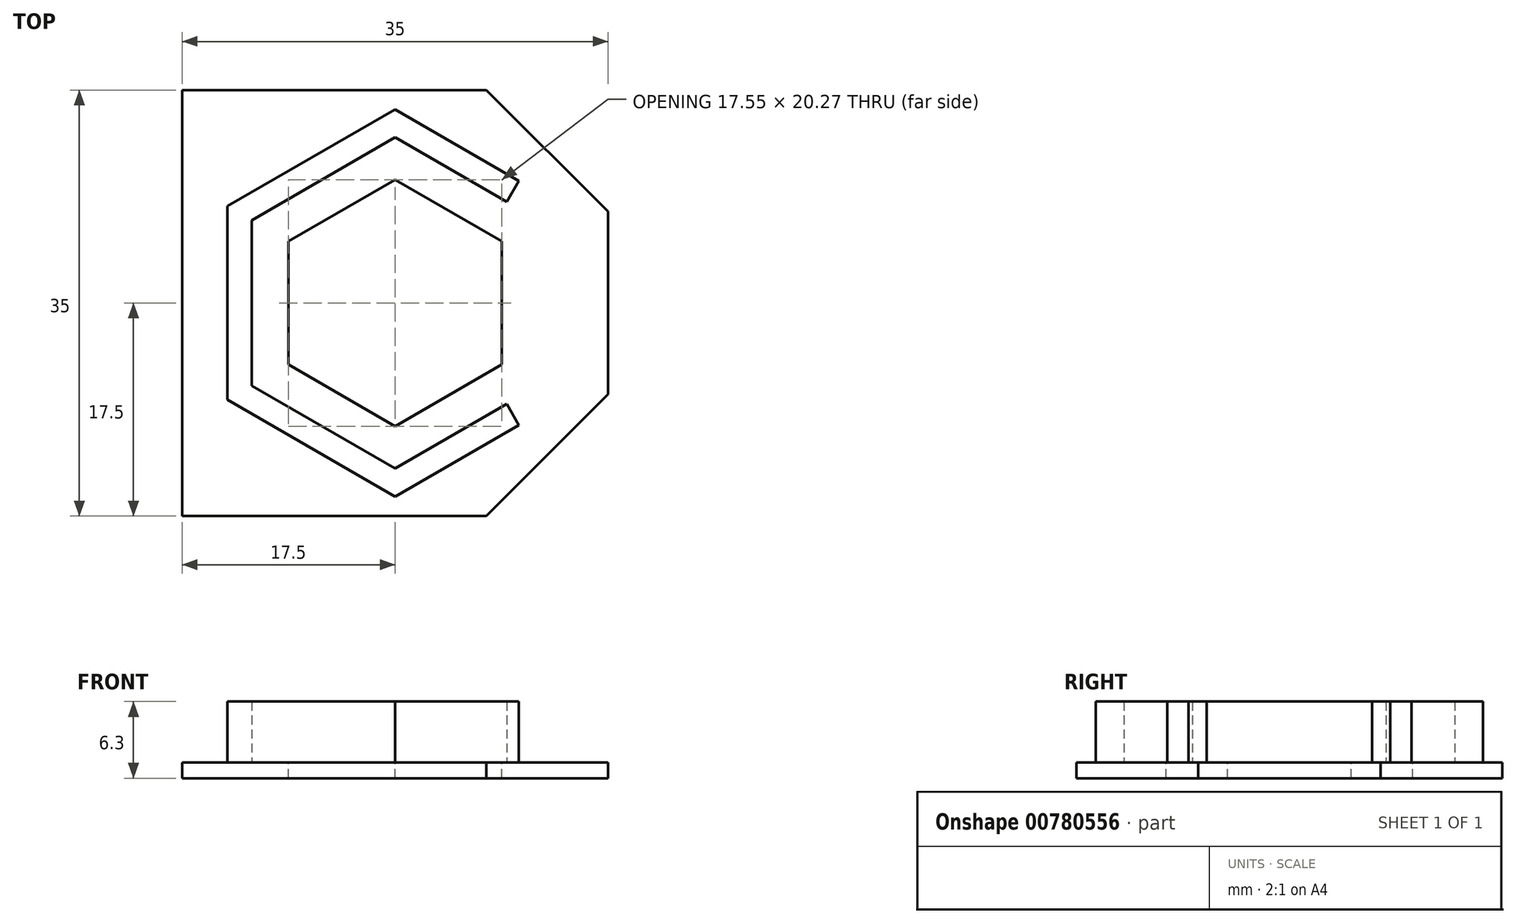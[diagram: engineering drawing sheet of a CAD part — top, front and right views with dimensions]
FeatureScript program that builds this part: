
annotation { "Feature Type Name" : "Feature", "Feature Type Description" : "" }
export const myFeature = defineFeature(function(context is Context, id is Id, definition is map)
    precondition{}
    {
        {
            var Q0;
            Q0=qCreatedBy(makeId("Top.planeOp"),FACE);
            var sketch = newSketch(context, id + "F0", { "sketchPlane" : qUnion([Q0])});
            skLineSegment(sketch, "E0.bottom", {"start": v(0, 0) * mm, "end": v(35, 0) * mm});
            skLineSegment(sketch, "E0.top", {"start": v(0, 35) * mm, "end": v(35, 35) * mm});
            skLineSegment(sketch, "E0.left", {"start": v(0, 0) * mm, "end": v(0, 35) * mm});
            skLineSegment(sketch, "E0.right", {"start": v(35, 0) * mm, "end": v(35, 35) * mm});
            skSolve(sketch);
        }
        {
            var Q0;
            Q0=makeQuery(id+"F0.imprint","IMPRINT",FACE,{"disambiguationData":[TD([[makeQuery(id+"F0.imprint","IMPRINT",EDGE,{"derivedFrom":sQuery(id+"F0.wireOp",EDGE,"E0.bottom")}),1.0]])]});
            extrude(context, id + "F1", {"entities" : qUnion([Q0]), "depth" : 2.6 / 2 * mm, "offsetDistance" : 25 * mm});
        }
        {
            var Q0;
            Q0=makeQuery(id+"F1.opExtrude","CAP_FACE",FACE,{"disambiguationData":[OSD([sQuery(id+"F0.wireOp",EDGE,"E0.bottom"),sQuery(id+"F0.wireOp",EDGE,"E0.top"),sQuery(id+"F0.wireOp",EDGE,"E0.left"),sQuery(id+"F0.wireOp",EDGE,"E0.right")])],"isStart":false});
            var sketch = newSketch(context, id + "F2", { "sketchPlane" : qUnion([Q0])});
            skCircle(sketch, "E1.cCircle", {"center": v(17.5, 17.5) * mm, "radius": 8.78 * mm, "construction": true});
            skLineSegment(sketch, "E1.0", {"start": v(17.5, 27.63) * mm, "end": v(26.28, 22.57) * mm});
            skLineSegment(sketch, "E1.1", {"start": v(26.27, 22.57) * mm, "end": v(26.27, 12.43) * mm});
            skLineSegment(sketch, "E1.2", {"start": v(26.27, 12.43) * mm, "end": v(17.5, 7.37) * mm});
            skLineSegment(sketch, "E1.3", {"start": v(17.5, 7.37) * mm, "end": v(8.73, 12.43) * mm});
            skLineSegment(sketch, "E1.4", {"start": v(8.73, 12.43) * mm, "end": v(8.73, 22.57) * mm});
            skLineSegment(sketch, "E1.5", {"start": v(8.73, 22.57) * mm, "end": v(17.5, 27.63) * mm});
            skPoint(sketch, "E1.0.midPoint", {"position": v(21.89, 25.1) * mm});
            skLineSegment(sketch, "E2.0", {"start": v(5.73, 24.3) * mm, "end": v(17.5, 31.1) * mm});
            skLineSegment(sketch, "E2.1", {"start": v(29.28, 24.3) * mm, "end": v(29.28, 10.7) * mm});
            skLineSegment(sketch, "E2.2", {"start": v(29.28, 10.7) * mm, "end": v(17.5, 3.9) * mm});
            skLineSegment(sketch, "E2.3", {"start": v(17.5, 31.1) * mm, "end": v(29.28, 24.3) * mm});
            skLineSegment(sketch, "E2.4", {"start": v(17.5, 3.9) * mm, "end": v(5.73, 10.7) * mm});
            skLineSegment(sketch, "E2.5", {"start": v(5.73, 10.7) * mm, "end": v(5.73, 24.3) * mm});
            skLineSegment(sketch, "E3.0", {"start": v(3.73, 25.45) * mm, "end": v(17.5, 33.4) * mm});
            skLineSegment(sketch, "E3.1", {"start": v(31.28, 25.45) * mm, "end": v(31.28, 9.55) * mm});
            skLineSegment(sketch, "E3.2", {"start": v(31.27, 9.55) * mm, "end": v(17.5, 1.6) * mm});
            skLineSegment(sketch, "E3.3", {"start": v(17.5, 33.4) * mm, "end": v(31.28, 25.45) * mm});
            skLineSegment(sketch, "E3.4", {"start": v(17.5, 1.6) * mm, "end": v(3.73, 9.55) * mm});
            skLineSegment(sketch, "E3.5", {"start": v(3.73, 9.55) * mm, "end": v(3.73, 25.45) * mm});
            skLineSegment(sketch, "E4", {"start": v(26.68, 25.8) * mm, "end": v(27.68, 27.53) * mm});
            skLineSegment(sketch, "E5", {"start": v(26.68, 9.2) * mm, "end": v(27.68, 7.47) * mm});
            skLineSegment(sketch, "E6", {"start": v(17.5, 35) * mm, "end": v(17.5, 0) * mm, "construction": true});
            skSolve(sketch);
        }
        {
            var Q0;
            Q0=makeQuery(id+"F2.imprint","IMPRINT",FACE,{"disambiguationData":[TD([[makeQuery(id+"F2.imprint","IMPRINT",EDGE,{"derivedFrom":sQuery(id+"F2.wireOp",EDGE,"E1.0")}),-1.0]])]});
            extrude(context, id + "F3", {"entities" : qUnion([Q0]), "operationType" : NewBodyOperationType.REMOVE, "oppositeDirection" : true, "depth" : 25 * mm, "offsetDistance" : 25 * mm});
        }
        {
            var Q0;
            {var subQ6=sQuery(id+"F2.wireOp",EDGE,"E2.0");Q0=makeQuery(id+"F2.imprint","IMPRINT",FACE,{"disambiguationData":[TD([[makeQuery(id+"F2.imprint","IMPRINT",EDGE,{"derivedFrom":subQ6}),1.0]])]});}
            extrude(context, id + "F4", {"entities" : qUnion([Q0]), "operationType" : NewBodyOperationType.ADD, "depth" : 5 * mm, "offsetDistance" : 25 * mm});
        }
        {
            var Q0;
            Q0=makeQuery(id+"F1.opExtrude","SWEPT_EDGE",EDGE,{"disambiguationData":[OSD([sQuery(id+"F0.wireOp",EDGE,"E0.bottom"),sQuery(id+"F0.wireOp",EDGE,"E0.right")])]});
            var Q1;
            Q1=makeQuery(id+"F1.opExtrude","SWEPT_EDGE",EDGE,{"disambiguationData":[OSD([sQuery(id+"F0.wireOp",EDGE,"E0.top"),sQuery(id+"F0.wireOp",EDGE,"E0.right")])]});
            chamfer(context, id + "F5", {"entities" : qUnion([Q0, Q1]), "width" : 10 * mm, "tangentPropagation" : true});
        }
    });
